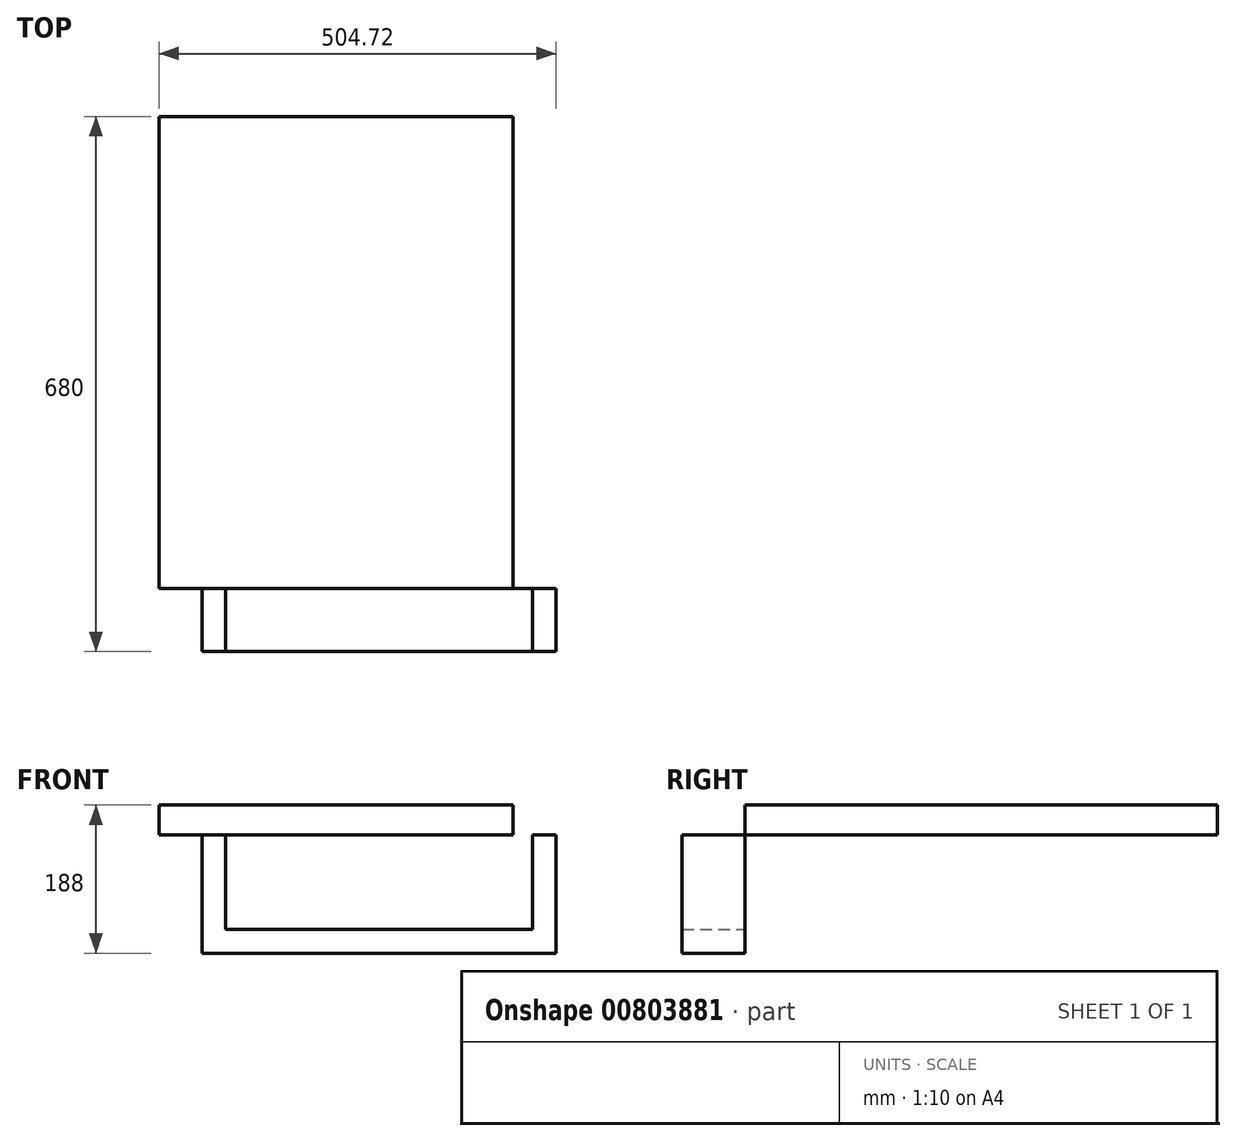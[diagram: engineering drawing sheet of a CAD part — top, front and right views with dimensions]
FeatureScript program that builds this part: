
annotation { "Feature Type Name" : "Feature", "Feature Type Description" : "" }
export const myFeature = defineFeature(function(context is Context, id is Id, definition is map)
    precondition{}
    {
        {
            var Q0;
            Q0=qCreatedBy(makeId("Top.planeOp"),FACE);
            var sketch = newSketch(context, id + "F0", { "sketchPlane" : qUnion([Q0])});
            skLineSegment(sketch, "E0.bottom", {"start": v(0, 0) * mm, "end": v(450, 0) * mm});
            skLineSegment(sketch, "E0.top", {"start": v(0, 600) * mm, "end": v(450, 600) * mm});
            skLineSegment(sketch, "E0.left", {"start": v(0, 0) * mm, "end": v(0, 600) * mm});
            skLineSegment(sketch, "E0.right", {"start": v(450, 0) * mm, "end": v(450, 600) * mm});
            skSolve(sketch);
        }
        {
            var Q0;
            Q0 = qSketchRegion(id + "F0", true);
            extrude(context, id + "F1", {"entities" : qUnion([Q0]), "depth" : 38 * mm, "offsetDistance" : 25 * mm});
        }
        {
            var Q0;
            Q0=qCreatedBy(makeId("Front.planeOp"),FACE);
            var sketch = newSketch(context, id + "F2", { "sketchPlane" : qUnion([Q0])});
            skLineSegment(sketch, "E1", {"start": v(54.72, 0) * mm, "end": v(84.72, 0) * mm});
            skLineSegment(sketch, "E2", {"start": v(84.72, 0) * mm, "end": v(84.72, -120) * mm});
            skLineSegment(sketch, "E3", {"start": v(84.72, -120) * mm, "end": v(474.72, -120) * mm});
            skLineSegment(sketch, "E4", {"start": v(474.72, -120) * mm, "end": v(474.72, 0) * mm});
            skLineSegment(sketch, "E5", {"start": v(474.72, 0) * mm, "end": v(504.72, 0) * mm});
            skLineSegment(sketch, "E6", {"start": v(504.72, 0) * mm, "end": v(504.72, -150) * mm});
            skLineSegment(sketch, "E7", {"start": v(504.72, -150) * mm, "end": v(54.72, -150) * mm});
            skLineSegment(sketch, "E8", {"start": v(54.72, -150) * mm, "end": v(54.72, 0) * mm});
            skSolve(sketch);
        }
        {
            var Q0;
            Q0=makeQuery(id+"F2.imprint","IMPRINT",FACE,{"disambiguationData":[TD([[makeQuery(id+"F2.imprint","IMPRINT",EDGE,{"derivedFrom":sQuery(id+"F2.wireOp",EDGE,"E1")}),-1.0]])]});
            extrude(context, id + "F3", {"entities" : qUnion([Q0]), "depth" : 80 * mm, "offsetDistance" : 25 * mm});
        }
    });
